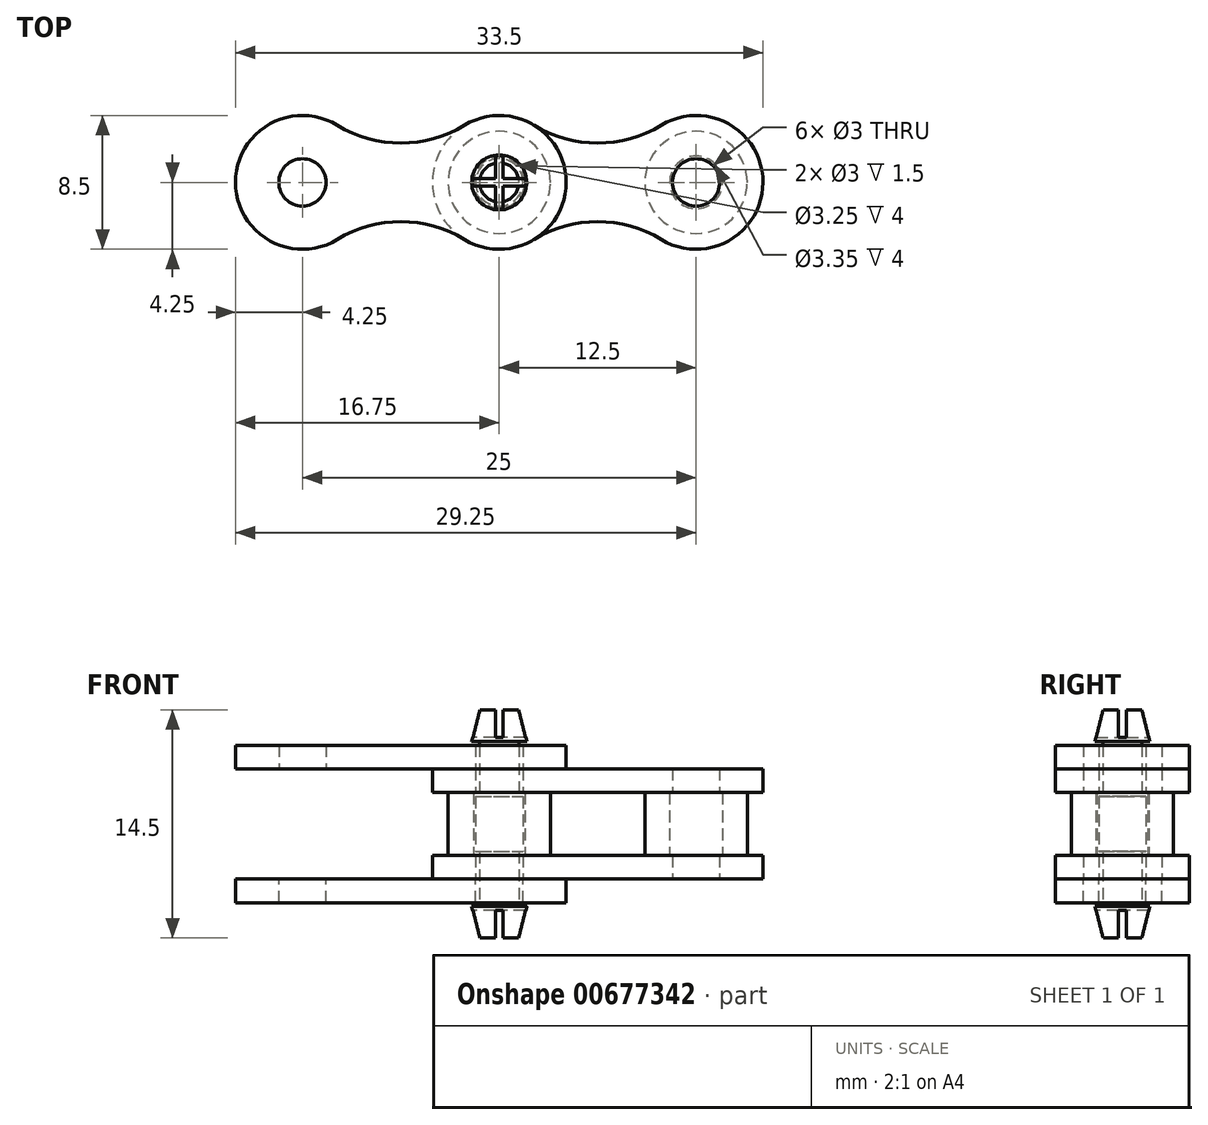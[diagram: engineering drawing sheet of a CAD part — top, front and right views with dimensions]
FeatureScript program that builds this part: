
annotation { "Feature Type Name" : "Feature", "Feature Type Description" : "" }
export const myFeature = defineFeature(function(context is Context, id is Id, definition is map)
    precondition{}
    {
        {
            var Q0;
            Q0=qCreatedBy(makeId("Top.planeOp"),FACE);
            var sketch = newSketch(context, id + "F0", { "sketchPlane" : qUnion([Q0])});
            skArc(sketch, "E0", {"start": v(2.21, 3.63) * mm, "mid": v(-4.25, 0) * mm, "end": v(2.21, -3.63) * mm});
            skArc(sketch, "E1", {"start": v(10.29, -3.63) * mm, "mid": v(16.75, 0) * mm, "end": v(10.29, 3.63) * mm});
            skArc(sketch, "E2", {"start": v(10.29, -3.63) * mm, "mid": v(6.25, -2.5) * mm, "end": v(2.21, -3.63) * mm});
            skArc(sketch, "E3.MirrorCS", {"start": v(10.29, 3.63) * mm, "mid": v(6.25, 2.5) * mm, "end": v(2.21, 3.63) * mm});
            skCircle(sketch, "E4", {"center": v(0, 0) * mm, "radius": 1.5 * mm});
            skCircle(sketch, "E5", {"center": v(12.5, 0) * mm, "radius": 1.5 * mm});
            skLineSegment(sketch, "E6", {"start": v(12.5, 0) * mm, "end": v(0, 0) * mm, "construction": true});
            skLineSegment(sketch, "E7", {"start": v(6.25, 0) * mm, "end": v(6.25, 25.3) * mm, "construction": true});
            skLineSegment(sketch, "E8", {"start": v(6.25, 0) * mm, "end": v(-6.25, 0) * mm, "construction": true});
            skLineSegment(sketch, "E9", {"start": v(-6.25, 0) * mm, "end": v(-6.25, 25.3) * mm, "construction": true});
            skLineSegment(sketch, "E10.MirrorCS", {"start": v(6.25, 0) * mm, "end": v(18.75, 0) * mm, "construction": true});
            skLineSegment(sketch, "E11.MirrorCS", {"start": v(18.75, 0) * mm, "end": v(18.75, 25.3) * mm, "construction": true});
            skSolve(sketch);
        }
        {
            var Q0;
            {var subQ1=sQuery(id+"F0.wireOp",EDGE,"E0");Q0=makeQuery(id+"F0.imprint","IMPRINT",FACE,{"disambiguationData":[TD([[makeQuery(id+"F0.imprint","IMPRINT",EDGE,{"derivedFrom":subQ1}),1.0]])]});}
            extrude(context, id + "F1", {"entities" : qUnion([Q0]), "depth" : 1.5 * mm, "offsetDistance" : 25 * mm});
        }
        {
            var Q0;
            Q0=makeQuery(id+"F1.opExtrude","CAP_FACE",FACE,{"disambiguationData":[OSD([sQuery(id+"F0.wireOp",EDGE,"E0"),sQuery(id+"F0.wireOp",EDGE,"E1"),sQuery(id+"F0.wireOp",EDGE,"E2"),sQuery(id+"F0.wireOp",EDGE,"E3.MirrorCS"),sQuery(id+"F0.wireOp",EDGE,"E4"),sQuery(id+"F0.wireOp",EDGE,"E5")])],"isStart":false});
            var sketch = newSketch(context, id + "F2", { "sketchPlane" : qUnion([Q0])});
            skCircle(sketch, "E12", {"center": v(0, 0) * mm, "radius": 1.63 * mm});
            skCircle(sketch, "E13", {"center": v(0, 0) * mm, "radius": 3.25 * mm});
            skCircle(sketch, "E14", {"center": v(12.5, 0) * mm, "radius": 1.68 * mm});
            skCircle(sketch, "E15", {"center": v(12.5, 0) * mm, "radius": 3.25 * mm});
            skLineSegment(sketch, "E16", {"start": v(3.25, 0) * mm, "end": v(3.25, 25.2) * mm, "construction": true});
            skLineSegment(sketch, "E17", {"start": v(9.25, 0) * mm, "end": v(9.25, 25.2) * mm, "construction": true});
            skSolve(sketch);
        }
        {
            var Q0;
            Q0=makeQuery(id+"F2.imprint","IMPRINT",FACE,{"disambiguationData":[TD([[makeQuery(id+"F2.imprint","IMPRINT",EDGE,{"derivedFrom":sQuery(id+"F2.wireOp",EDGE,"E12")}),-1.0]])]});
            var Q1;
            Q1=makeQuery(id+"F2.imprint","IMPRINT",FACE,{"disambiguationData":[TD([[makeQuery(id+"F2.imprint","IMPRINT",EDGE,{"derivedFrom":sQuery(id+"F2.wireOp",EDGE,"E14")}),-1.0]])]});
            extrude(context, id + "F3", {"entities" : qUnion([Q0, Q1]), "depth" : 4 * mm, "offsetDistance" : 25 * mm});
        }
        {
            var Q0;
            Q0=makeQuery(id+"F3.opExtrude","CAP_FACE",FACE,{"disambiguationData":[OSD([sQuery(id+"F2.wireOp",EDGE,"E12"),sQuery(id+"F2.wireOp",EDGE,"E13")])],"isStart":false});
            var sketch = newSketch(context, id + "F4", { "sketchPlane" : qUnion([Q0])});
            skArc(sketch, "E18", {"start": v(2.21, 3.63) * mm, "mid": v(-4.25, 0) * mm, "end": v(2.21, -3.63) * mm});
            skArc(sketch, "E19", {"start": v(10.29, -3.63) * mm, "mid": v(16.75, 0) * mm, "end": v(10.29, 3.63) * mm});
            skArc(sketch, "E20", {"start": v(10.29, -3.63) * mm, "mid": v(6.25, -2.5) * mm, "end": v(2.21, -3.63) * mm});
            skArc(sketch, "E21.MirrorCS", {"start": v(10.29, 3.63) * mm, "mid": v(6.25, 2.5) * mm, "end": v(2.21, 3.63) * mm});
            skCircle(sketch, "E22", {"center": v(0, 0) * mm, "radius": 1.5 * mm});
            skCircle(sketch, "E23", {"center": v(12.5, 0) * mm, "radius": 1.5 * mm});
            skSolve(sketch);
        }
        {
            var Q0;
            Q0=qSketchRegion(id+"F4",true);
            extrude(context, id + "F5", {"entities" : qUnion([Q0]), "operationType" : NewBodyOperationType.ADD, "depth" : 1.5 * mm, "offsetDistance" : 25 * mm});
        }
        {
            var Q0;
            Q0=makeQuery(id+"F5.opExtrude","CAP_FACE",FACE,{"disambiguationData":[OSD([sQuery(id+"F4.wireOp",EDGE,"E18"),sQuery(id+"F4.wireOp",EDGE,"E19"),sQuery(id+"F4.wireOp",EDGE,"E20"),sQuery(id+"F4.wireOp",EDGE,"E21.MirrorCS"),sQuery(id+"F4.wireOp",EDGE,"E22"),sQuery(id+"F4.wireOp",EDGE,"E23")])],"isStart":false});
            var sketch = newSketch(context, id + "F6", { "sketchPlane" : qUnion([Q0])});
            skArc(sketch, "E24", {"start": v(-10.29, 3.63) * mm, "mid": v(-16.75, 0) * mm, "end": v(-10.29, -3.63) * mm});
            skArc(sketch, "E25", {"start": v(-2.21, -3.63) * mm, "mid": v(4.25, 0) * mm, "end": v(-2.21, 3.63) * mm});
            skArc(sketch, "E26", {"start": v(-2.21, -3.63) * mm, "mid": v(-6.25, -2.5) * mm, "end": v(-10.29, -3.63) * mm});
            skArc(sketch, "E27.MirrorCS", {"start": v(-2.21, 3.63) * mm, "mid": v(-6.25, 2.5) * mm, "end": v(-10.29, 3.63) * mm});
            skCircle(sketch, "E28", {"center": v(-12.5, 0) * mm, "radius": 1.5 * mm});
            skCircle(sketch, "E29", {"center": v(0, 0) * mm, "radius": 1.5 * mm});
            skSolve(sketch);
        }
        {
            var Q0;
            Q0=makeQuery(id+"F6.imprint","IMPRINT",FACE,{"disambiguationData":[TD([[makeQuery(id+"F6.imprint","IMPRINT",EDGE,{"derivedFrom":sQuery(id+"F6.wireOp",EDGE,"E24")}),1.0]])]});
            var Q1;
            Q1=makeQuery(id+"F6.imprint","IMPRINT",FACE,{"disambiguationData":[TD([[makeQuery(id+"F6.imprint","IMPRINT",EDGE,{"derivedFrom":sQuery(id+"F6.wireOp",EDGE,"E29")}),-1.0]])]});
            extrude(context, id + "F7", {"entities" : qUnion([Q0, Q1]), "depth" : 1.5 * mm, "offsetDistance" : 25 * mm});
        }
        {
            var Q0;
            Q0=makeQuery(id+"F0.imprint","IMPRINT",FACE,{"disambiguationData":[TD([[makeQuery(id+"F0.imprint","IMPRINT",EDGE,{"derivedFrom":sQuery(id+"F0.wireOp",EDGE,"E0")}),1.0]])]});
            var sketch = newSketch(context, id + "F8", { "sketchPlane" : qUnion([Q0])});
            skArc(sketch, "E30", {"start": v(-10.29, 3.63) * mm, "mid": v(-16.75, 0) * mm, "end": v(-10.29, -3.63) * mm});
            skArc(sketch, "E31", {"start": v(-2.21, -3.63) * mm, "mid": v(4.25, 0) * mm, "end": v(-2.21, 3.63) * mm});
            skArc(sketch, "E32", {"start": v(-2.21, -3.63) * mm, "mid": v(-6.25, -2.5) * mm, "end": v(-10.29, -3.63) * mm});
            skArc(sketch, "E33.MirrorCS", {"start": v(-2.21, 3.63) * mm, "mid": v(-6.25, 2.5) * mm, "end": v(-10.29, 3.63) * mm});
            skCircle(sketch, "E34", {"center": v(-12.5, 0) * mm, "radius": 1.5 * mm});
            skCircle(sketch, "E35", {"center": v(0, 0) * mm, "radius": 1.5 * mm});
            skSolve(sketch);
        }
        {
            var Q0;
            Q0=makeQuery(id+"F8.imprint","IMPRINT",FACE,{"disambiguationData":[TD([[makeQuery(id+"F8.imprint","IMPRINT",EDGE,{"derivedFrom":sQuery(id+"F8.wireOp",EDGE,"E30")}),1.0]])]});
            var Q1;
            Q1=makeQuery(id+"F8.imprint","IMPRINT",FACE,{"disambiguationData":[TD([[makeQuery(id+"F8.imprint","IMPRINT",EDGE,{"derivedFrom":sQuery(id+"F8.wireOp",EDGE,"E35")}),-1.0]])]});
            extrude(context, id + "F9", {"entities" : qUnion([Q0, Q1]), "oppositeDirection" : true, "depth" : 1.5 * mm, "offsetDistance" : 25 * mm});
        }
        {
            var Q0;
            Q0=qCreatedBy(makeId("Front.planeOp"),FACE);
            var sketch = newSketch(context, id + "F10", { "sketchPlane" : qUnion([Q0])});
            skLineSegment(sketch, "E36", {"start": v(0, 10.75) * mm, "end": v(1.25, 10.75) * mm});
            skLineSegment(sketch, "E37", {"start": v(1.25, 8.75) * mm, "end": v(1.75, 8.75) * mm});
            skLineSegment(sketch, "E38", {"start": v(1.75, 8.75) * mm, "end": v(1.25, 10.75) * mm});
            skLineSegment(sketch, "E39", {"start": v(1.25, 8.75) * mm, "end": v(1.25, 5.25) * mm});
            skLineSegment(sketch, "E40", {"start": v(1.25, 5.25) * mm, "end": v(1.5, 5.25) * mm});
            skLineSegment(sketch, "E41", {"start": v(1.5, 5.25) * mm, "end": v(1.5, 3.5) * mm});
            skLineSegment(sketch, "E42.MirrorCS", {"start": v(1.25, 1.75) * mm, "end": v(1.5, 1.75) * mm});
            skLineSegment(sketch, "E43.MirrorCS", {"start": v(1.25, -1.75) * mm, "end": v(1.75, -1.75) * mm});
            skLineSegment(sketch, "E44.MirrorCS", {"start": v(1.5, 1.75) * mm, "end": v(1.5, 3.5) * mm});
            skLineSegment(sketch, "E45.MirrorCS", {"start": v(0, -3.75) * mm, "end": v(1.25, -3.75) * mm});
            skLineSegment(sketch, "E46.MirrorCS", {"start": v(1.75, -1.75) * mm, "end": v(1.25, -3.75) * mm});
            skLineSegment(sketch, "E47.MirrorCS", {"start": v(1.25, -1.75) * mm, "end": v(1.25, 1.75) * mm});
            skLineSegment(sketch, "E48", {"start": v(0, -3.75) * mm, "end": v(0, 10.75) * mm});
            skLineSegment(sketch, "E49", {"start": v(0, 10.75) * mm, "end": v(0, -3.75) * mm, "construction": true});
            skSolve(sketch);
        }
        {
            var Q0;
            Q0=makeQuery(id+"F10.imprint","IMPRINT",FACE,{"disambiguationData":[TD([[makeQuery(id+"F10.imprint","IMPRINT",EDGE,{"derivedFrom":sQuery(id+"F10.wireOp",EDGE,"E36")}),-1.0]])]});
            var Q1;
            Q1=sQuery(id+"F10.wireOp",EDGE,"E38");
            var Q2;
            Q2=sQuery(id+"F10.wireOp",EDGE,"E37");
            var Q3;
            Q3=sQuery(id+"F10.wireOp",EDGE,"E39");
            var Q4;
            Q4=sQuery(id+"F10.wireOp",EDGE,"E40");
            var Q5;
            Q5=sQuery(id+"F10.wireOp",EDGE,"E41");
            var Q6;
            Q6=sQuery(id+"F10.wireOp",EDGE,"E44.MirrorCS");
            var Q7;
            Q7=sQuery(id+"F10.wireOp",EDGE,"E42.MirrorCS");
            var Q8;
            Q8=sQuery(id+"F10.wireOp",EDGE,"E47.MirrorCS");
            var Q9;
            Q9=sQuery(id+"F10.wireOp",EDGE,"E43.MirrorCS");
            var Q10;
            Q10=sQuery(id+"F10.wireOp",EDGE,"E46.MirrorCS");
            var Q11;
            Q11=sQuery(id+"F10.wireOp",EDGE,"E45.MirrorCS");
            var Q12;
            Q12=sQuery(id+"F10.wireOp",EDGE,"E36");
            var Q13;
            Q13=sQuery(id+"F10.wireOp",EDGE,"E48");
            revolve(context, id + "F11", {"entities" : qUnion([Q0]), "surfaceEntities" : qUnion([Q1, Q2, Q3, Q4, Q5, Q6, Q7, Q8, Q9, Q10, Q11, Q12]), "axis" : qUnion([Q13]), "revolveType" : RevolveType.FULL});
        }
        {
            var Q0;
            Q0=makeQuery(id+"F11.opRevolve","SWEPT_FACE",FACE,{"disambiguationData":[OSD([sQuery(id+"F10.wireOp",EDGE,"E36")])]});
            var sketch = newSketch(context, id + "F12", { "sketchPlane" : qUnion([Q0])});
            skLineSegment(sketch, "E50.bottom", {"start": v(1.88, 0.25) * mm, "end": v(0.25, 0.25) * mm});
            skLineSegment(sketch, "E50.top", {"start": v(1.88, -0.25) * mm, "end": v(0.25, -0.25) * mm});
            skLineSegment(sketch, "E50.left", {"start": v(1.88, 0.25) * mm, "end": v(1.88, -0.25) * mm});
            skLineSegment(sketch, "E50.right", {"start": v(-1.88, 0.25) * mm, "end": v(-1.88, -0.25) * mm});
            skPoint(sketch, "E50.middle", {"position": v(0, 0) * mm});
            skLineSegment(sketch, "E51.bottom", {"start": v(0.25, -1.88) * mm, "end": v(-0.25, -1.88) * mm});
            skLineSegment(sketch, "E51.top", {"start": v(0.25, 1.88) * mm, "end": v(-0.25, 1.88) * mm});
            skLineSegment(sketch, "E51.left", {"start": v(0.25, -1.88) * mm, "end": v(0.25, -0.25) * mm});
            skLineSegment(sketch, "E51.right", {"start": v(-0.25, -1.88) * mm, "end": v(-0.25, -0.25) * mm});
            skLineSegment(sketch, "E52.trimOffspring", {"start": v(-0.25, 0.25) * mm, "end": v(-0.25, 1.88) * mm});
            skLineSegment(sketch, "E53.trimOffspring", {"start": v(-0.25, -0.25) * mm, "end": v(-1.88, -0.25) * mm});
            skLineSegment(sketch, "E54.trimOffspring", {"start": v(0.25, 0.25) * mm, "end": v(0.25, 1.88) * mm});
            skLineSegment(sketch, "E55.trimOffspring", {"start": v(-0.25, 0.25) * mm, "end": v(-1.88, 0.25) * mm});
            skSolve(sketch);
        }
        {
            var Q0;
            {var subQ0=sQuery(id+"F12.wireOp",EDGE,"E50.bottom");var subQ5=sQuery(id+"F12.wireOp",EDGE,"E54.trimOffspring");var subQ6=makeQuery(id+"F12.imprint","INTERSECT",VERTEX,{"derivedFrom":[subQ0,subQ5]});Q0=makeQuery(id+"F12.imprint","IMPRINT",FACE,{"disambiguationData":[TD([[makeQuery(id+"F12.imprint","IMPRINT",EDGE,{"disambiguationData":[TD([[subQ6,1.0]])],"derivedFrom":subQ0}),1.0]])]});}
            var Q1;
            {var subQ0=sQuery(id+"F12.wireOp",EDGE,"E51.top");Q1=makeQuery(id+"F12.imprint","IMPRINT",FACE,{"disambiguationData":[TD([[makeQuery(id+"F12.imprint","IMPRINT",EDGE,{"derivedFrom":subQ0}),1.0]])]});}
            var Q2;
            {var subQ0=sQuery(id+"F12.wireOp",EDGE,"E50.left");Q2=makeQuery(id+"F12.imprint","IMPRINT",FACE,{"disambiguationData":[TD([[makeQuery(id+"F12.imprint","IMPRINT",EDGE,{"derivedFrom":subQ0}),-1.0]])]});}
            var Q3;
            {var subQ0=sQuery(id+"F12.wireOp",EDGE,"E51.bottom");Q3=makeQuery(id+"F12.imprint","IMPRINT",FACE,{"disambiguationData":[TD([[makeQuery(id+"F12.imprint","IMPRINT",EDGE,{"derivedFrom":subQ0}),-1.0]])]});}
            var Q4;
            {var subQ0=sQuery(id+"F12.wireOp",EDGE,"E50.right");Q4=makeQuery(id+"F12.imprint","IMPRINT",FACE,{"disambiguationData":[TD([[makeQuery(id+"F12.imprint","IMPRINT",EDGE,{"derivedFrom":subQ0}),1.0]])]});}
            extrude(context, id + "F13", {"entities" : qUnion([Q0, Q1, Q2, Q3, Q4]), "oppositeDirection" : true, "depth" : 1.75 * mm, "offsetDistance" : 25 * mm});
        }
        {
            var Q0;
            Q0=makeQuery(id+"F13.opExtrude","SWEPT_BODY",BODY,{"disambiguationData":[OSD([sQuery(id+"F12.wireOp",EDGE,"E50.bottom"),sQuery(id+"F12.wireOp",EDGE,"E50.top"),sQuery(id+"F12.wireOp",EDGE,"E50.left"),sQuery(id+"F12.wireOp",EDGE,"E50.right"),sQuery(id+"F12.wireOp",EDGE,"E51.bottom"),sQuery(id+"F12.wireOp",EDGE,"E51.top"),sQuery(id+"F12.wireOp",EDGE,"E51.left"),sQuery(id+"F12.wireOp",EDGE,"E51.right"),sQuery(id+"F12.wireOp",EDGE,"E52.trimOffspring"),sQuery(id+"F12.wireOp",EDGE,"E53.trimOffspring"),sQuery(id+"F12.wireOp",EDGE,"E54.trimOffspring"),sQuery(id+"F12.wireOp",EDGE,"E55.trimOffspring")])]});
            var Q1;
            Q1=makeQuery(id+"F11.opRevolve","SWEPT_BODY",BODY,{"disambiguationData":[OSD([sQuery(id+"F10.wireOp",EDGE,"E36"),sQuery(id+"F10.wireOp",EDGE,"E37"),sQuery(id+"F10.wireOp",EDGE,"E38"),sQuery(id+"F10.wireOp",EDGE,"E39"),sQuery(id+"F10.wireOp",EDGE,"E40"),sQuery(id+"F10.wireOp",EDGE,"E41"),sQuery(id+"F10.wireOp",EDGE,"E42.MirrorCS"),sQuery(id+"F10.wireOp",EDGE,"E43.MirrorCS"),sQuery(id+"F10.wireOp",EDGE,"E44.MirrorCS"),sQuery(id+"F10.wireOp",EDGE,"E45.MirrorCS"),sQuery(id+"F10.wireOp",EDGE,"E46.MirrorCS"),sQuery(id+"F10.wireOp",EDGE,"E47.MirrorCS"),sQuery(id+"F10.wireOp",EDGE,"E48")])]});
            booleanBodies(context, id + "F14", {"operationType" : BooleanOperationType.SUBTRACTION, "tools" : qUnion([Q0]), "targets" : qUnion([Q1])});
        }
        {
            var Q0;
            Q0=makeQuery(id+"F11.opRevolve","SWEPT_FACE",FACE,{"disambiguationData":[OSD([sQuery(id+"F10.wireOp",EDGE,"E45.MirrorCS")])]});
            var sketch = newSketch(context, id + "F15", { "sketchPlane" : qUnion([Q0])});
            skLineSegment(sketch, "E56.bottom", {"start": v(1.88, 0.25) * mm, "end": v(0.25, 0.25) * mm});
            skLineSegment(sketch, "E56.top", {"start": v(1.88, -0.25) * mm, "end": v(0.25, -0.25) * mm});
            skLineSegment(sketch, "E56.left", {"start": v(1.88, 0.25) * mm, "end": v(1.88, -0.25) * mm});
            skLineSegment(sketch, "E56.right", {"start": v(-1.88, 0.25) * mm, "end": v(-1.88, -0.25) * mm});
            skPoint(sketch, "E56.middle", {"position": v(0, 0) * mm});
            skLineSegment(sketch, "E57.bottom", {"start": v(0.25, -1.88) * mm, "end": v(-0.25, -1.88) * mm});
            skLineSegment(sketch, "E57.top", {"start": v(0.25, 1.88) * mm, "end": v(-0.25, 1.88) * mm});
            skLineSegment(sketch, "E57.left", {"start": v(0.25, -1.88) * mm, "end": v(0.25, -0.25) * mm});
            skLineSegment(sketch, "E57.right", {"start": v(-0.25, -1.88) * mm, "end": v(-0.25, -0.25) * mm});
            skLineSegment(sketch, "E58.trimOffspring", {"start": v(-0.25, 0.25) * mm, "end": v(-0.25, 1.88) * mm});
            skLineSegment(sketch, "E59.trimOffspring", {"start": v(-0.25, -0.25) * mm, "end": v(-1.88, -0.25) * mm});
            skLineSegment(sketch, "E60.trimOffspring", {"start": v(0.25, 0.25) * mm, "end": v(0.25, 1.88) * mm});
            skLineSegment(sketch, "E61.trimOffspring", {"start": v(-0.25, 0.25) * mm, "end": v(-1.88, 0.25) * mm});
            skSolve(sketch);
        }
        {
            var Q0;
            {var subQ0=sQuery(id+"F15.wireOp",EDGE,"E56.bottom");var subQ5=sQuery(id+"F15.wireOp",EDGE,"E60.trimOffspring");var subQ6=makeQuery(id+"F15.imprint","INTERSECT",VERTEX,{"derivedFrom":[subQ0,subQ5]});Q0=makeQuery(id+"F15.imprint","IMPRINT",FACE,{"disambiguationData":[TD([[makeQuery(id+"F15.imprint","IMPRINT",EDGE,{"disambiguationData":[TD([[subQ6,1.0]])],"derivedFrom":subQ0}),1.0]])]});}
            var Q1;
            {var subQ0=sQuery(id+"F15.wireOp",EDGE,"E56.left");Q1=makeQuery(id+"F15.imprint","IMPRINT",FACE,{"disambiguationData":[TD([[makeQuery(id+"F15.imprint","IMPRINT",EDGE,{"derivedFrom":subQ0}),-1.0]])]});}
            var Q2;
            {var subQ0=sQuery(id+"F15.wireOp",EDGE,"E57.bottom");Q2=makeQuery(id+"F15.imprint","IMPRINT",FACE,{"disambiguationData":[TD([[makeQuery(id+"F15.imprint","IMPRINT",EDGE,{"derivedFrom":subQ0}),-1.0]])]});}
            var Q3;
            {var subQ0=sQuery(id+"F15.wireOp",EDGE,"E56.right");Q3=makeQuery(id+"F15.imprint","IMPRINT",FACE,{"disambiguationData":[TD([[makeQuery(id+"F15.imprint","IMPRINT",EDGE,{"derivedFrom":subQ0}),1.0]])]});}
            var Q4;
            {var subQ0=sQuery(id+"F15.wireOp",EDGE,"E57.top");Q4=makeQuery(id+"F15.imprint","IMPRINT",FACE,{"disambiguationData":[TD([[makeQuery(id+"F15.imprint","IMPRINT",EDGE,{"derivedFrom":subQ0}),1.0]])]});}
            extrude(context, id + "F16", {"entities" : qUnion([Q0, Q1, Q2, Q3, Q4]), "oppositeDirection" : true, "depth" : 1.75 * mm, "offsetDistance" : 25 * mm});
        }
        {
            var Q0;
            Q0=makeQuery(id+"F16.opExtrude","SWEPT_BODY",BODY,{"disambiguationData":[OSD([sQuery(id+"F15.wireOp",EDGE,"E56.bottom"),sQuery(id+"F15.wireOp",EDGE,"E56.top"),sQuery(id+"F15.wireOp",EDGE,"E56.left"),sQuery(id+"F15.wireOp",EDGE,"E56.right"),sQuery(id+"F15.wireOp",EDGE,"E57.bottom"),sQuery(id+"F15.wireOp",EDGE,"E57.top"),sQuery(id+"F15.wireOp",EDGE,"E57.left"),sQuery(id+"F15.wireOp",EDGE,"E57.right"),sQuery(id+"F15.wireOp",EDGE,"E58.trimOffspring"),sQuery(id+"F15.wireOp",EDGE,"E59.trimOffspring"),sQuery(id+"F15.wireOp",EDGE,"E60.trimOffspring"),sQuery(id+"F15.wireOp",EDGE,"E61.trimOffspring")])]});
            var Q1;
            Q1=makeQuery(id+"F11.opRevolve","SWEPT_BODY",BODY,{"disambiguationData":[OSD([sQuery(id+"F10.wireOp",EDGE,"E36"),sQuery(id+"F10.wireOp",EDGE,"E37"),sQuery(id+"F10.wireOp",EDGE,"E38"),sQuery(id+"F10.wireOp",EDGE,"E39"),sQuery(id+"F10.wireOp",EDGE,"E40"),sQuery(id+"F10.wireOp",EDGE,"E41"),sQuery(id+"F10.wireOp",EDGE,"E42.MirrorCS"),sQuery(id+"F10.wireOp",EDGE,"E43.MirrorCS"),sQuery(id+"F10.wireOp",EDGE,"E44.MirrorCS"),sQuery(id+"F10.wireOp",EDGE,"E45.MirrorCS"),sQuery(id+"F10.wireOp",EDGE,"E46.MirrorCS"),sQuery(id+"F10.wireOp",EDGE,"E47.MirrorCS"),sQuery(id+"F10.wireOp",EDGE,"E48")])]});
            booleanBodies(context, id + "F17", {"operationType" : BooleanOperationType.SUBTRACTION, "tools" : qUnion([Q0]), "targets" : qUnion([Q1])});
        }
    });
